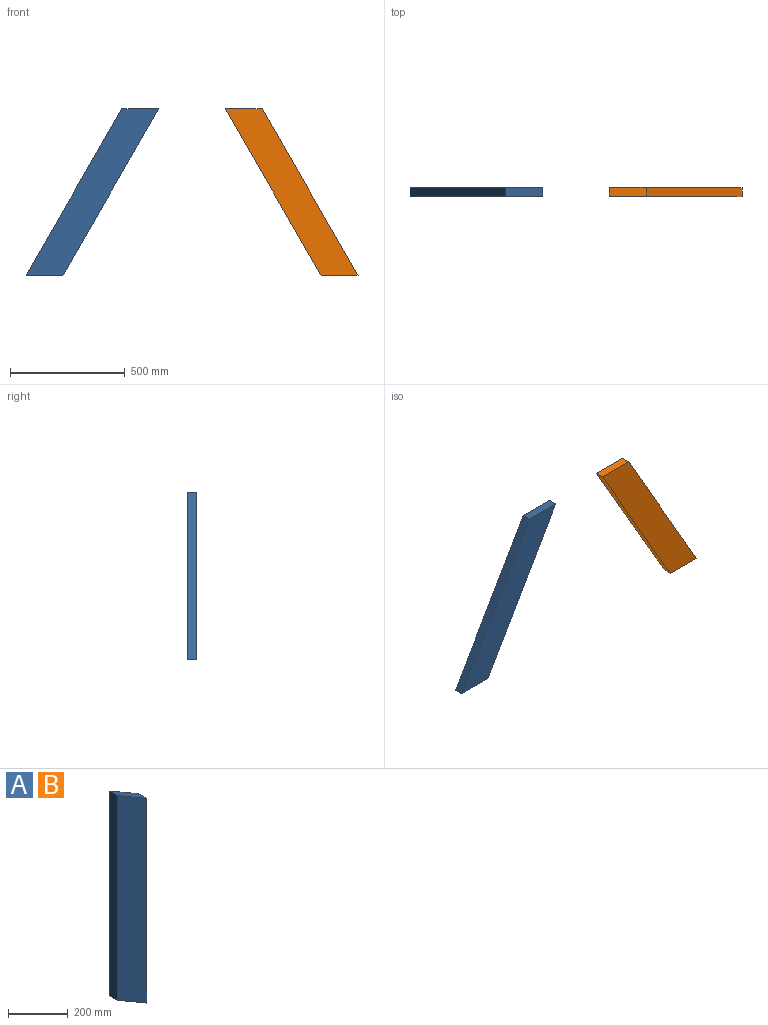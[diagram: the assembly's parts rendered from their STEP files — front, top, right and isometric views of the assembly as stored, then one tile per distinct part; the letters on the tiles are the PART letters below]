
ASSEMBLY  parts=2 mates=1
PART A: 6 faces, bbox 139.7x38.1x916.5 mm
  f0: plane 835.89x38.1mm, normal (-1,0,0), area 31847.3mm2, adj f1,f3,f4,f5
  f1: plane 139.7x80.66mm, normal (-0.5,0,-0.87), area 6146mm2, adj f0,f2,f4,f5
  f2: plane 835.89x38.1mm, normal (1,0,0), area 31847.3mm2, adj f1,f3,f4,f5
  f3: plane 139.7x80.66mm, normal (0.5,0,0.87), area 6146mm2, adj f0,f2,f4,f5
  f4: plane 916.54x139.7mm, normal (0,-1,0), area 116773.5mm2, adj f0,f1,f2,f3
  f5: plane 916.54x139.7mm, normal (0,1,0), area 116773.5mm2, adj f0,f1,f2,f3
PART B: same geometry as A
PLACE A rot(axis=(-0.26,0,-0.97),180deg) t=(-1054.9,-38.1,215.38)mm
PLACE B rot(axis=(0,-1,0),30deg) t=(70.07,0,215.38)mm
MATE planar A.f3 <-> B.f3  axis (0,0,1) through (-717.61,-19.05,939.28)mm
